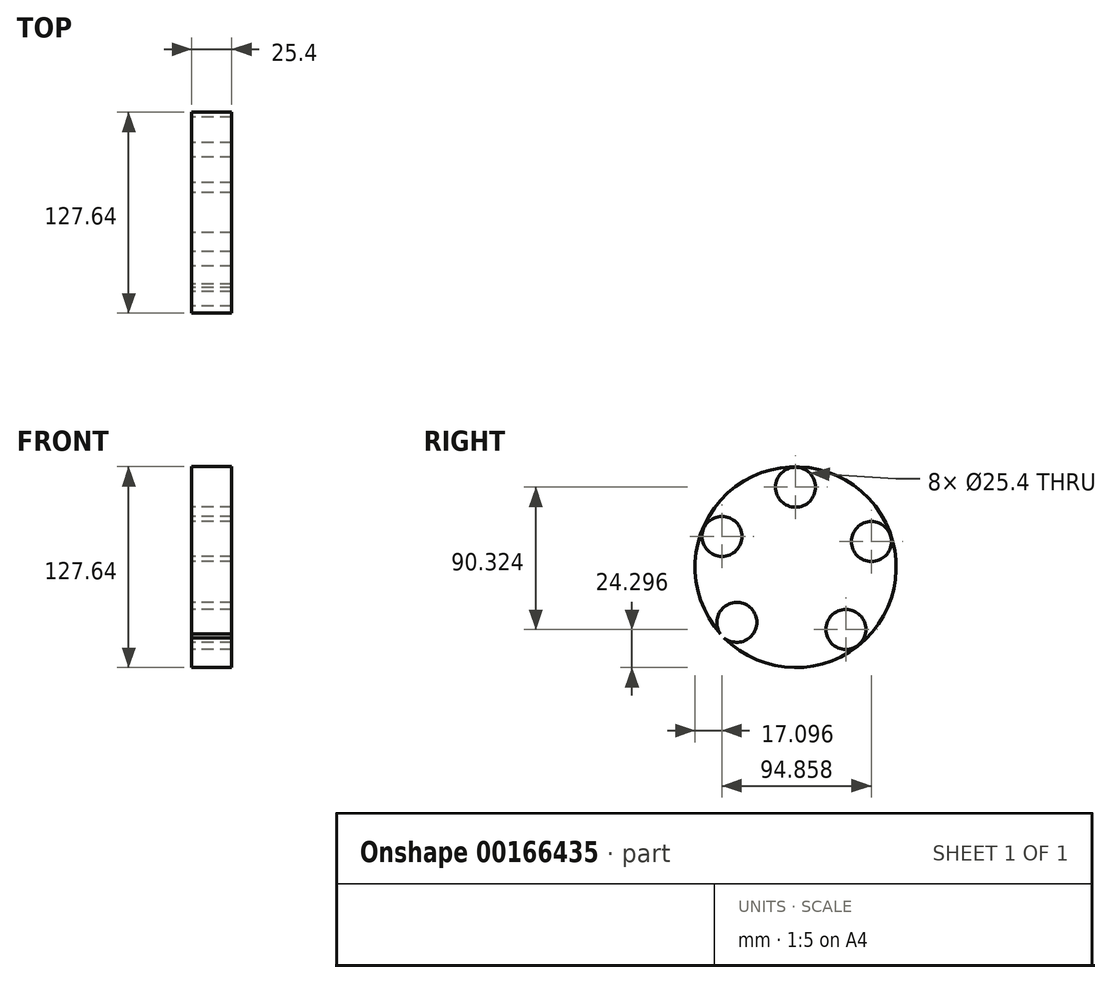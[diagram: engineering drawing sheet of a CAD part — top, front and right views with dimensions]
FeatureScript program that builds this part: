
annotation { "Feature Type Name" : "Feature", "Feature Type Description" : "" }
export const myFeature = defineFeature(function(context is Context, id is Id, definition is map)
    precondition{}
    {
        {
            var Q0;
            Q0=qCreatedBy(makeId("Right.planeOp"),FACE);
            var sketch = newSketch(context, id + "F0", { "sketchPlane" : qUnion([Q0])});
            skCircle(sketch, "E0", {"center": v(0, 0) * mm, "radius": 63.82 * mm});
            skCircle(sketch, "E1", {"center": v(0, 50.8) * mm, "radius": 12.7 * mm});
            skCircle(sketch, "E2", {"center": v(48.13, 16.24) * mm, "radius": 12.7 * mm});
            skCircle(sketch, "E3", {"center": v(31.91, -39.52) * mm, "radius": 12.7 * mm});
            skCircle(sketch, "E4", {"center": v(-37.32, -35.04) * mm, "radius": 12.7 * mm});
            skCircle(sketch, "E5", {"center": v(-46.72, 19.57) * mm, "radius": 12.7 * mm});
            skSolve(sketch);
        }
        {
            var Q0;
            Q0=makeQuery(id+"F0.imprint","IMPRINT",FACE,{"disambiguationData":[TD([[makeQuery(id+"F0.imprint","IMPRINT",EDGE,{"derivedFrom":sQuery(id+"F0.wireOp",EDGE,"E1")}),-1.0]])]});
            extrude(context, id + "F1", {"entities" : qUnion([Q0]), "endBound" : BoundingType.SYMMETRIC, "depth" : 25.4 * mm});
        }
    });
